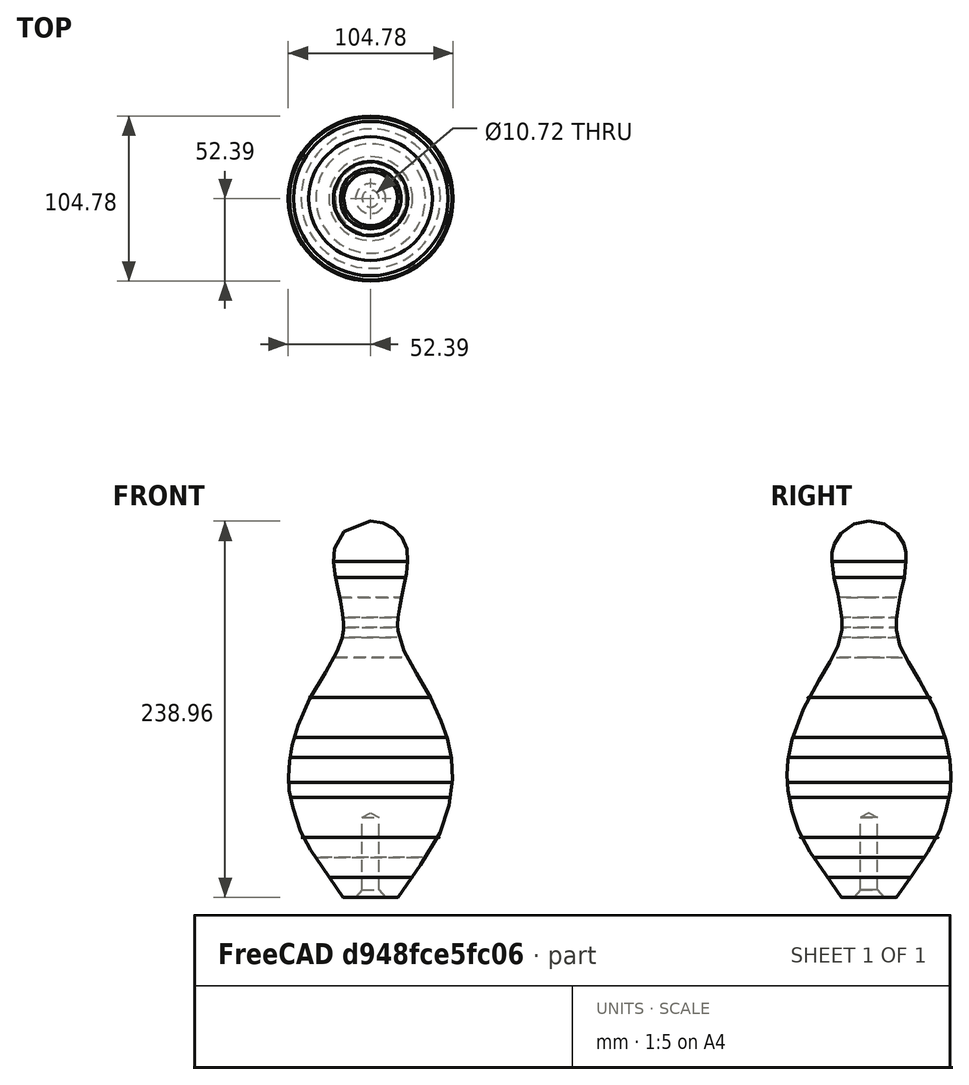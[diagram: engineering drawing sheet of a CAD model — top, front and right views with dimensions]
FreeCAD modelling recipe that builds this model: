
FCSTD DOCUMENT  (FreeCAD 0.21R33771 (Git))
Label: duckpin
License: All rights reserved
LicenseURL: http://en.wikipedia.org/wiki/All_rights_reserved
objects: Sketcher::SketchObject×1, Part::Revolution×1
note: 2 computed .brp shape members not serialized (recipe doc carries the construction recipe); baked Part::Feature solids carry a one-line shape summary decoded from their .brp

FEATURE [Sketcher::SketchObject] Sketch
  FullyConstrained = false
  MapMode = 5
  Placement = pos=(0,0,0) rot=(1,0,0;1.5708rad)
  sketch-geometry (58):
    g0: GeomPoint X=-17.4625 Y=0 Z=0
    g1: GeomPoint X=-26.5906 Y=12.7 Z=0
    g2: GeomPoint X=-34.7266 Y=25.4 Z=0
    g3: GeomPoint X=-44.2516 Y=38.1 Z=0
    g4: GeomPoint X=-51.3954 Y=63.5 Z=0
    g5: GeomPoint X=-52.3875 Y=73.025 Z=0
    g6: GeomPoint X=-51.5938 Y=88.9 Z=0
    g7: GeomPoint X=-49.0141 Y=101.6 Z=0
    g8: GeomPoint X=-39.2906 Y=127 Z=0
    g9: GeomPoint X=-22.4235 Y=152.4 Z=0
    g10: GeomPoint X=-17.4625 Y=165.1 Z=0
    g11: GeomPoint X=-17.0656 Y=171.45 Z=0
    g12: GeomPoint X=-17.2641 Y=177.8 Z=0
    g13: GeomPoint X=-19.2484 Y=190.5 Z=0
    g14: GeomPoint X=-22.6219 Y=203.2 Z=0
    g15: GeomPoint X=-23.6141 Y=213.519 Z=0
    g16-g34: Circle x19 (B-spline internal-alignment scaffolding for g35; pole/knot coordinates omitted)
    g35: BSplineCurve PolesCount=19 KnotsCount=17 Degree=3 IsPeriodic=0
    g36-g52: GeomPoint x17 (B-spline internal-alignment scaffolding for g35; pole/knot coordinates omitted)
    g53: LineSegment StartX=-17.4625 StartY=0 StartZ=0 EndX=-9.525 EndY=0 EndZ=0
    g54: LineSegment StartX=-5.35781 StartY=4.7625 StartZ=0 EndX=-5.35781 EndY=50.8 EndZ=0
    g55: LineSegment StartX=-5.35781 StartY=50.8 StartZ=0 EndX=0 EndY=53.6488 EndZ=0
    g56: LineSegment StartX=0 StartY=53.6488 StartZ=0 EndX=0 EndY=238.955 EndZ=0
    g57: LineSegment StartX=-5.35781 StartY=4.7625 StartZ=0 EndX=-9.525 EndY=0 EndZ=0
  constraints (82):
    c: DistanceX(g0,g-1) = 17.4625
    c: DistanceX(g1,g-1) = 26.5906
    c: DistanceX(g2,g-1) = 34.7266
    c: DistanceY(g-1,g1) = 12.7
    c: DistanceY(g-1,g2) = 25.4
    c: DistanceY(g-1,g3) = 38.1
    c: DistanceY(g-1,g4) = 63.5
    c: DistanceY(g-1,g5) = 73.025
    c: DistanceY(g-1,g6) = 88.9
    c: DistanceY(g-1,g7) = 101.6
    c: DistanceY(g-1,g8) = 127
    c: DistanceY(g-1,g9) = 152.4
    c: DistanceY(g-1,g10) = 165.1
    c: DistanceY(g-1,g11) = 171.45
    c: DistanceY(g-1,g12) = 177.8
    c: DistanceY(g-1,g13) = 190.5
    c: DistanceY(g-1,g14) = 203.2
    c: DistanceY(g-1,g15) = 213.519
    c: DistanceX(g3,g-1) = 44.2516
    c: DistanceX(g4,g-1) = 51.3954
    c: DistanceX(g5,g-1) = 52.3875
    c: DistanceX(g6,g-1) = 51.5938
    c: DistanceX(g7,g-1) = 49.0141
    c: DistanceX(g8,g-1) = 39.2906
    c: DistanceX(g9,g-1) = 22.4235
    c: DistanceX(g10,g-1) = 17.4625
    c: DistanceX(g11,g-1) = 17.0656
    c: DistanceX(g12,g-1) = 17.2641
    c: DistanceX(g13,g-1) = 19.2484
    c: DistanceX(g14,g-1) = 22.6219
    c: DistanceX(g15,g-1) = 23.6141
    c: Coincident(g35,g0)
    c: Equal(g16,g17)
    c: Coincident(g17,g1)
    c: Equal(g16,g18)
    c: Coincident(g18,g2)
    c: Equal(g16,g19)
    c: Coincident(g19,g3)
    c: Equal(g16,g20)
    c: Coincident(g20,g4)
    c: Equal(g16,g21)
    c: Coincident(g21,g5)
    c: Equal(g16,g22)
    c: Coincident(g22,g6)
    c: Equal(g16,g23)
    c: Coincident(g23,g7)
    c: Equal(g16,g24)
    c: Coincident(g24,g8)
    c: Equal(g16,g25)
    c: Coincident(g25,g9)
    c: Equal(g16,g26)
    c: Coincident(g26,g10)
    c: Equal(g16,g27)
    c: Coincident(g27,g11)
    c: Equal(g16,g28)
    c: Coincident(g28,g12)
    c: Equal(g16,g29)
    c: Coincident(g29,g13)
    c: Equal(g16,g30)
    c: Coincident(g30,g14)
    c: Equal(g16,g31)
    c: Coincident(g31,g15)
    c: Equal(g16,g32)
    c: Equal(g16,g33)
    c: InternalAlignment(g16-g34 -> g35) x19
    c: InternalAlignment(g36-g52 -> g35) x17
    c: PointOnObject(g35,g-2)
    c: Coincident(g53,g0)
    c: PointOnObject(g53,g-1)
    c: Horizontal(g53)
    c: Vertical(g54)
    c: Coincident(g55,g54)
    c: PointOnObject(g55,g-2)
    c: Coincident(g56,g55)
    c: Coincident(g56,g35)
    c: DistanceX(g53,g-1) = 9.525
    c: DistanceX(g54,g-1) = 5.35781
    c: DistanceY(g-1,g54) = 4.7625
    c: Coincident(g57,g54)
    c: Coincident(g57,g53)
    c: DistanceY(g-1,g54) = 50.8
    c: Angle(g54,g55) = 2.05949
FEATURE [Part::Revolution] Revolve
  Angle = 360
  Axis = (0,0,1)
  Base = (0,0,0)
  FaceMakerClass = Part::FaceMakerBullseye
  Solid = false
  Source = -> Sketch
  Symmetric = false
